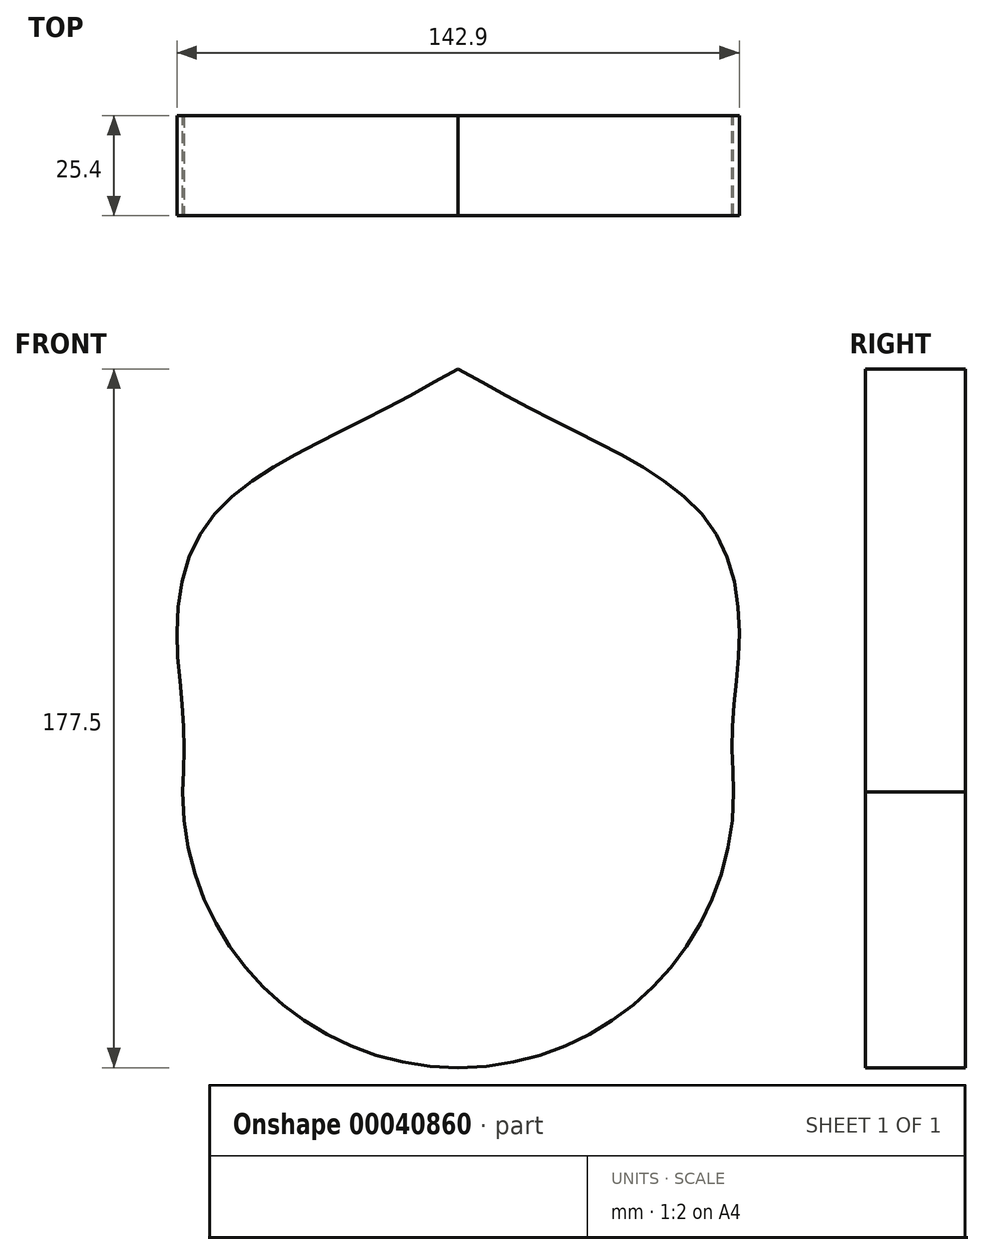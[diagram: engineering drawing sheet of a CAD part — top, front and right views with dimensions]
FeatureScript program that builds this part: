
annotation { "Feature Type Name" : "Feature", "Feature Type Description" : "" }
export const myFeature = defineFeature(function(context is Context, id is Id, definition is map)
    precondition{}
    {
        {
            var Q0;
            Q0=qCreatedBy(makeId("Front.planeOp"),FACE);
            var sketch = newSketch(context, id + "F0", { "sketchPlane" : qUnion([Q0])});
            skFitSpline(sketch, "E0", {"points": [v(70, 0) * mm, v(69.8, 18.7) * mm, v(71.45, 41.25) * mm, v(65.57, 65.57) * mm, v(47.5, 82.27) * mm, v(25.18, 93.96) * mm, v(0, 107.5) * mm], "startDerivative": vector(-6.03, 124.92) * mm, "endDerivative": vector(-140.01, 77.56) * mm});
            skFitSpline(sketch, "E1.MirrorCS", {"points": [v(-70, 0) * mm, v(-69.8, 18.7) * mm, v(-71.45, 41.25) * mm, v(-65.57, 65.57) * mm, v(-47.5, 82.27) * mm, v(-25.18, 93.96) * mm, v(0, 107.5) * mm], "startDerivative": vector(6.03, 124.92) * mm, "endDerivative": vector(140.01, 77.56) * mm});
            skArc(sketch, "E2", {"start": v(-70, 0) * mm, "mid": v(0, -70) * mm, "end": v(70, 0) * mm});
            skPoint(sketch, "E3.endSnap0", {"position": v(0, -70) * mm});
            skLineSegment(sketch, "E4", {"start": v(182.15, 107.5) * mm, "end": v(182.15, -70) * mm});
            skPoint(sketch, "E5.orphan", {"position": v(207.55, -70) * mm});
            skPoint(sketch, "E3.start.orphan", {"position": v(0, -70) * mm});
            skLineSegment(sketch, "E6", {"start": v(182.15, -70) * mm, "end": v(207.55, -70) * mm});
            skLineSegment(sketch, "E7", {"start": v(182.15, 107.5) * mm, "end": v(207.55, 107.5) * mm});
            skLineSegment(sketch, "E8", {"start": v(207.55, 107.5) * mm, "end": v(207.55, -70) * mm});
            skSolve(sketch);
        }
        {
            var Q0;
            Q0=makeQuery(id+"F0.imprint","IMPRINT",FACE,{"disambiguationData":[TD([[makeQuery(id+"F0.imprint","IMPRINT",EDGE,{"derivedFrom":sQuery(id+"F0.wireOp",EDGE,"E0")}),1.0]])]});
            extrude(context, id + "F1", {"entities" : qUnion([Q0]), "depth" : 25.4 * mm});
        }
    });
